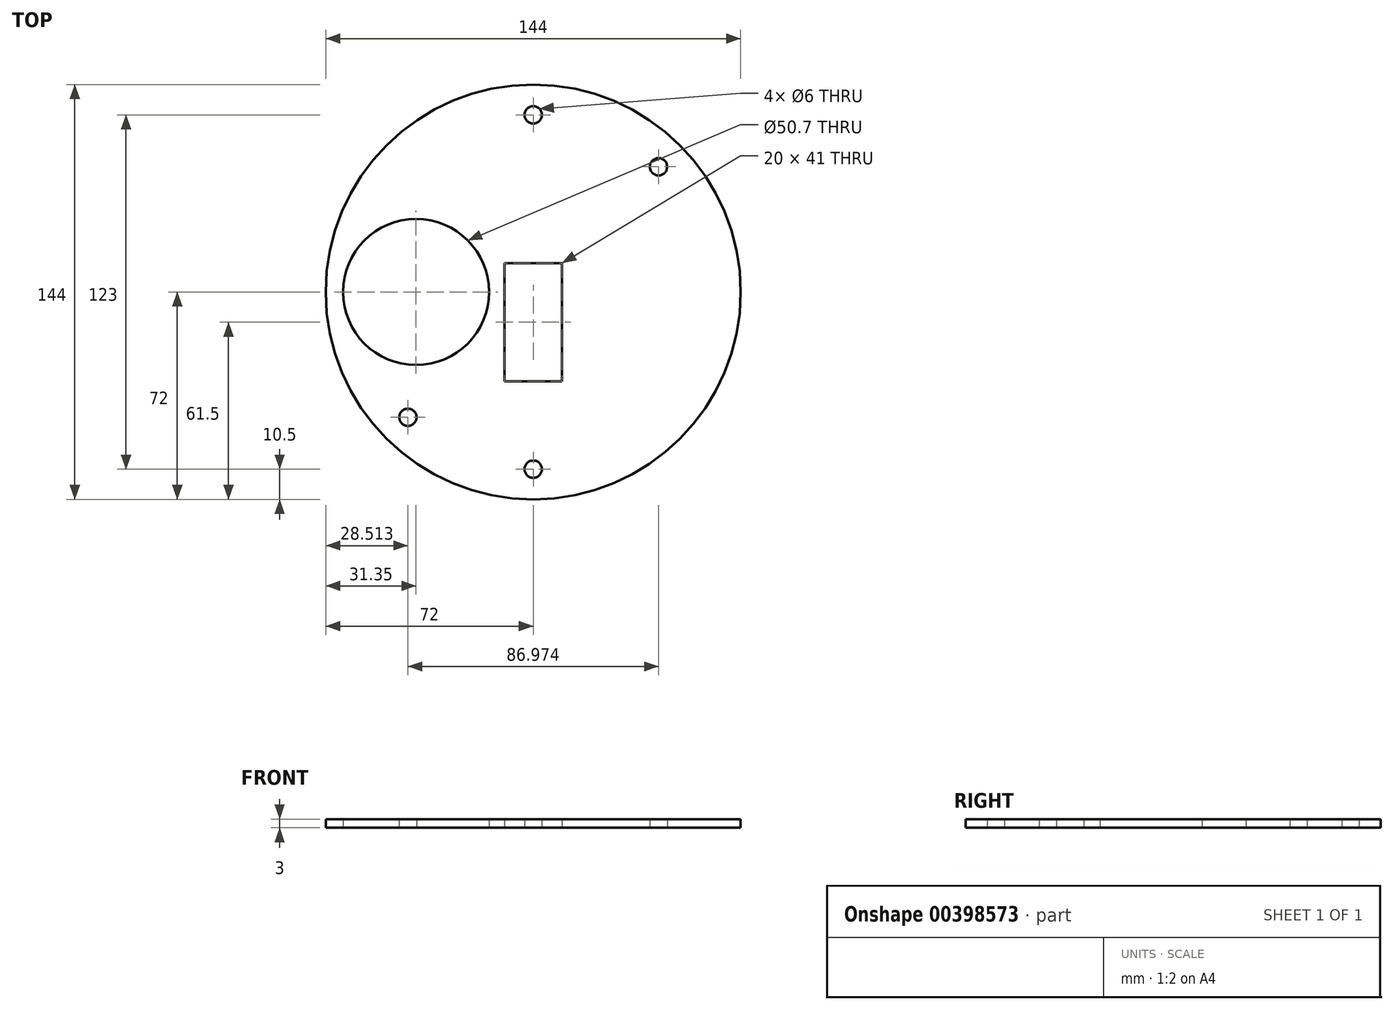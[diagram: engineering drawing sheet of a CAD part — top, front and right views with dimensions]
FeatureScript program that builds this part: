
annotation { "Feature Type Name" : "Feature", "Feature Type Description" : "" }
export const myFeature = defineFeature(function(context is Context, id is Id, definition is map)
    precondition{}
    {
        {
            var Q0;
            Q0=qCreatedBy(makeId("Top.planeOp"),FACE);
            var sketch = newSketch(context, id + "F0", { "sketchPlane" : qUnion([Q0])});
            skCircle(sketch, "E0", {"center": v(0, 0) * mm, "radius": 72 * mm});
            skCircle(sketch, "E1", {"center": v(-40.65, 0) * mm, "radius": 25.35 * mm});
            skCircle(sketch, "E2", {"center": v(0, 61.5) * mm, "radius": 3 * mm});
            skCircle(sketch, "E3.MirrorC", {"center": v(0, -61.5) * mm, "radius": 3 * mm});
            skLineSegment(sketch, "E4.bottom", {"start": v(-10, 10) * mm, "end": v(10, 10) * mm});
            skLineSegment(sketch, "E4.top", {"start": v(-10, -31) * mm, "end": v(10, -31) * mm});
            skLineSegment(sketch, "E4.left", {"start": v(-10, 10) * mm, "end": v(-10, -31) * mm});
            skLineSegment(sketch, "E4.right", {"start": v(10, 10) * mm, "end": v(10, -31) * mm});
            skCircle(sketch, "E5", {"center": v(43.49, 43.49) * mm, "radius": 3 * mm});
            skCircle(sketch, "E6", {"center": v(-43.49, -43.49) * mm, "radius": 3 * mm});
            skSolve(sketch);
        }
        {
            var Q0;
            Q0=makeQuery(id+"F0.imprint","IMPRINT",FACE,{"disambiguationData":[TD([[makeQuery(id+"F0.imprint","IMPRINT",EDGE,{"derivedFrom":sQuery(id+"F0.wireOp",EDGE,"E0")}),1.0]])]});
            extrude(context, id + "F1", {"entities" : qUnion([Q0]), "depth" : 3 * mm});
        }
    });
